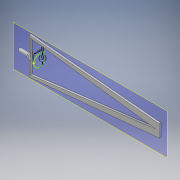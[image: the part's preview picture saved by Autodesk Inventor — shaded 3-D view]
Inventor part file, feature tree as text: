
AUTODESK INVENTOR PART (.ipt)
format: ipt  version: 2018 (Build 220112000, 112)  size: 205,312 bytes
history: native  units: mm
features: sketch x11, extrude x10, plane x1, projected_geometry x1
ambient origin geometry x8: Origin, YZ Plane, XZ Plane, XY Plane, X Axis, Y Axis, Z Axis, Center Point
bodies: Solid1 (feature_tree)
feature tree (23):
  extrude  "Extrusion1"  Depth=10.0mm TaperAngle=0.0deg
  sketch  "Sketch2"  dims[d3=9.0mm d4=8.0mm d5=10.0mm d6=0.0mm]
  extrude  "Extrusion2"  Depth=10.0mm TaperAngle=0.0deg
  extrude  "Extrusion3"  Depth=1.125mm
  extrude  "Extrusion4"  Depth=1.6mm
  extrude  "Extrusion5"  Depth=1.8mm
  extrude  "Extrusion6"  Depth=2.4mm
  extrude  "Extrusion7"  Depth=3.32mm
  extrude  "Extrusion8"  Depth=10.0mm
  extrude  "Extrusion9"  Depth=15.0mm TaperAngle=0.0deg
  plane  "Work Plane1"
  extrude  "Extrusion11"  Depth=1.175mm
  sketch  "Sketch1"  dims[d0=10.0mm d1=10.0mm d2=0.0mm]
  sketch  "Sketch3"  dims[d9=1.125mm d10=1.125mm]
  sketch  "Sketch4"  dims[d12=0.0mm d13=0.0mm d16=1.6mm]
  sketch  "Sketch5"  dims[d18=1.6mm d21=1.8mm]
  projected_geometry  "Projected Loop1"
  sketch  "Sketch6"  dims[d23=1.8mm d24=2.4mm]
  sketch  "Sketch7"  dims[d26=3.32mm d27=3.32mm]
  sketch  "Sketch8"  dims[d29=10.0mm d30=0.0mm d31=5.0mm]
  sketch  "Sketch9"  dims[d32=2.4mm d33=15.0mm d34=0.0mm]
  sketch  "Sketch10"  dims[d35=15.0mm d36=0.0mm d37=1.175mm]
  sketch  "Sketch12"  dims[d38=7.0mm d39=0.0mm d40=10.0mm d41=0.0mm d42=8.0mm d43=0.0mm d60=4.1mm d61=25.4mm d62=29.4mm d63=14.7mm d64=10.0mm d65=1.5mm d66=0.0mm d67=2.5mm]
